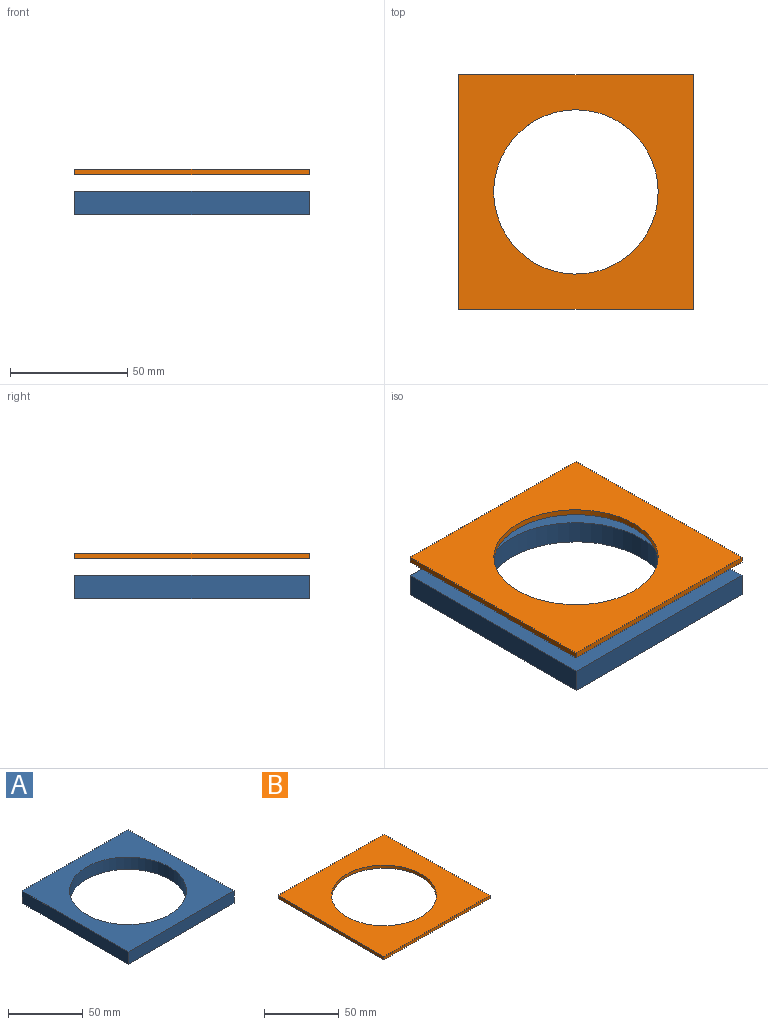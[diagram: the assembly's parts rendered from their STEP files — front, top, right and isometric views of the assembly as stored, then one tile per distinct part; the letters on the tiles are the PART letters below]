
ASSEMBLY  parts=2 mates=1
PART A: 7 faces, bbox 100x100x10 mm
  f0: plane 100x10mm, normal (-1,0,0), area 1000mm2, adj f1,f3,f5,f6
  f1: plane 100x10mm, normal (0,-1,0), area 1000mm2, adj f0,f2,f5,f6
  f2: plane 100x10mm, normal (1,0,0), area 1000mm2, adj f1,f3,f5,f6
  f3: plane 100x10mm, normal (0,1,0), area 1000mm2, adj f0,f2,f5,f6
  f4: cylinder r=39mm len=78mm, axis (0,0,-1), area 2450.4mm2, adj f5,f6
  f5: plane 100x100mm, normal (0,0,1), area 5221.6mm2, adj f0,f1,f2,f3,f4
  f6: plane 100x100mm, normal (0,0,-1), area 5221.6mm2, adj f0,f1,f2,f3,f4
PART B: 7 faces, bbox 100x100x2.5 mm
  f0: plane 100x2.5mm, normal (-1,0,0), area 250mm2, adj f1,f3,f5,f6
  f1: plane 100x2.5mm, normal (0,-1,0), area 250mm2, adj f0,f2,f5,f6
  f2: plane 100x2.5mm, normal (1,0,0), area 250mm2, adj f1,f3,f5,f6
  f3: plane 100x2.5mm, normal (0,1,0), area 250mm2, adj f0,f2,f5,f6
  f4: cylinder r=35mm len=70mm, axis (0,0,-1), area 549.8mm2, adj f5,f6
  f5: plane 100x100mm, normal (0,0,1), area 6151.5mm2, adj f0,f1,f2,f3,f4
  f6: plane 100x100mm, normal (0,0,-1), area 6151.5mm2, adj f0,f1,f2,f3,f4
PLACE A t=(6.29,11.54,25.27)mm
PLACE B t=(6.29,11.54,42.32)mm
MATE slider A.f4 <-> B.f4  axis (0,0,-1) through (56.29,61.54,25.27)mm
